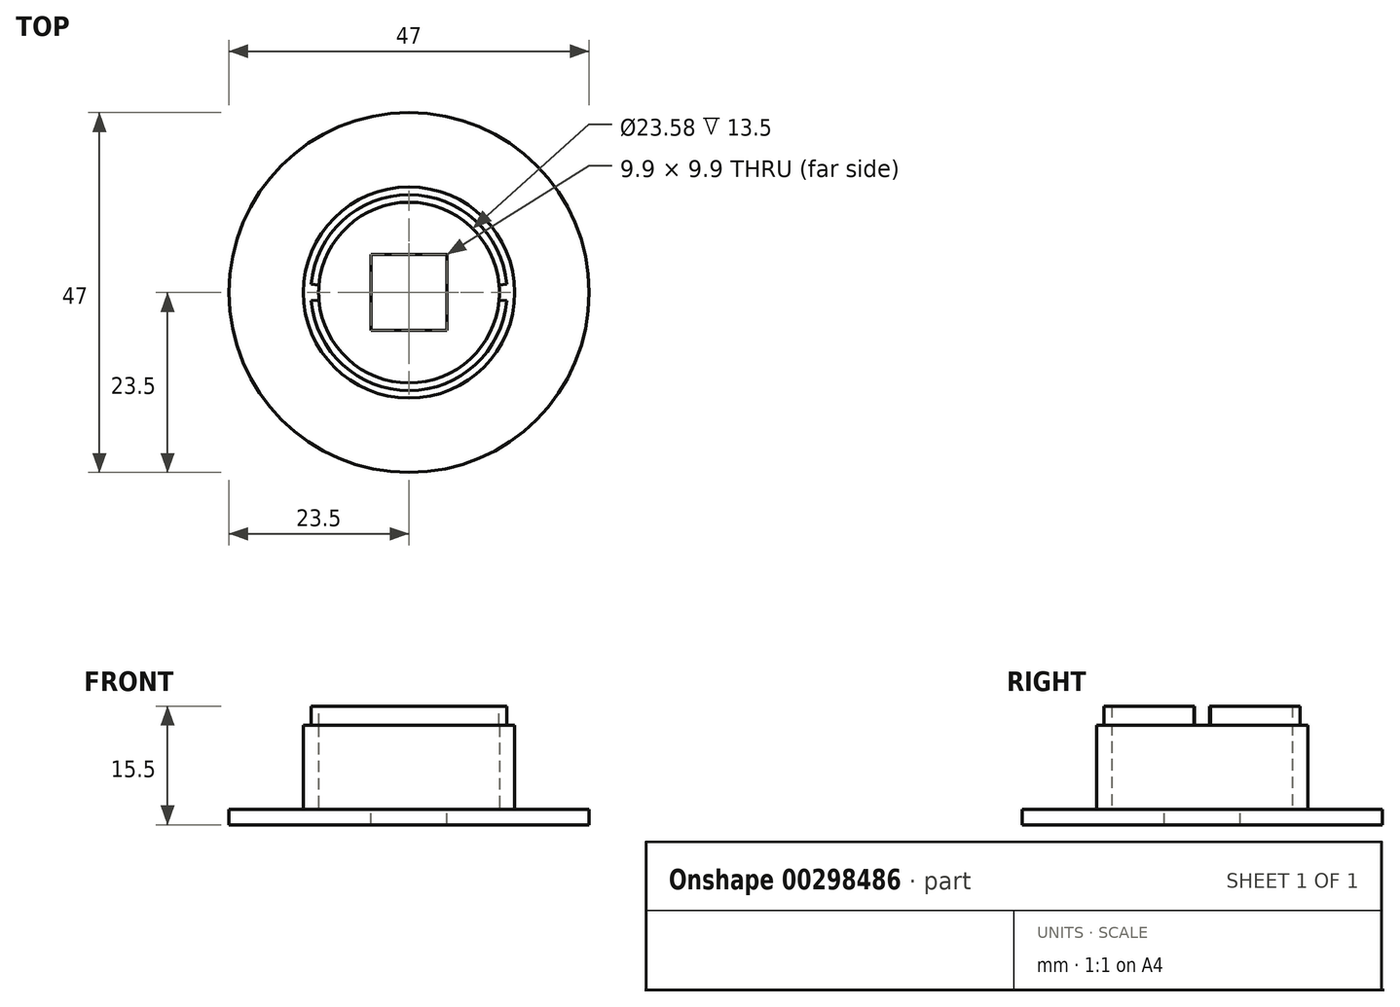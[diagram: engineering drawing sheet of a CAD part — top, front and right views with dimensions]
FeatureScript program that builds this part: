
annotation { "Feature Type Name" : "Feature", "Feature Type Description" : "" }
export const myFeature = defineFeature(function(context is Context, id is Id, definition is map)
    precondition{}
    {
        {
            var Q0;
            Q0=qCreatedBy(makeId("Front.planeOp"),FACE);
            var sketch = newSketch(context, id + "F0", { "sketchPlane" : qUnion([Q0])});
            skLineSegment(sketch, "E0", {"start": v(0, 0) * mm, "end": v(-23.5, 0) * mm});
            skLineSegment(sketch, "E1", {"start": v(-23.5, 0) * mm, "end": v(-23.5, 2) * mm});
            skLineSegment(sketch, "E2", {"start": v(-23.5, 2) * mm, "end": v(-13.8, 2) * mm});
            skLineSegment(sketch, "E3", {"start": v(-13.8, 2) * mm, "end": v(-13.8, 13) * mm});
            skLineSegment(sketch, "E4.top", {"start": v(-13.8, 13) * mm, "end": v(-12.8, 13) * mm});
            skLineSegment(sketch, "E4.right", {"start": v(-12.8, 15.5) * mm, "end": v(-12.8, 13) * mm});
            skLineSegment(sketch, "E5.0", {"start": v(-11.8, 15.5) * mm, "end": v(-11.8, 13) * mm});
            skLineSegment(sketch, "E6", {"start": v(-11.8, 13) * mm, "end": v(-11.8, 2) * mm});
            skLineSegment(sketch, "E7", {"start": v(-11.8, 2) * mm, "end": v(0, 2) * mm});
            skLineSegment(sketch, "E8", {"start": v(0, 0) * mm, "end": v(0, 2) * mm});
            skLineSegment(sketch, "E9", {"start": v(-12.8, 15.5) * mm, "end": v(-11.8, 15.5) * mm});
            skSolve(sketch);
        }
        {
            var Q0;
            Q0=makeQuery(id+"F0.imprint","IMPRINT",FACE,{"disambiguationData":[TD([[makeQuery(id+"F0.imprint","IMPRINT",EDGE,{"derivedFrom":sQuery(id+"F0.wireOp",EDGE,"E0")}),-1.0]])]});
            var Q1;
            Q1=sQuery(id+"F0.wireOp",EDGE,"E8");
            revolve(context, id + "F1", {"entities" : qUnion([Q0]), "axis" : qUnion([Q1]), "revolveType" : RevolveType.FULL});
        }
        {
            var Q0;
            Q0=makeQuery(id+"F1.opRevolve","SWEPT_FACE",FACE,{"disambiguationData":[OSD([sQuery(id+"F0.wireOp",EDGE,"E9")])]});
            var sketch = newSketch(context, id + "F2", { "sketchPlane" : qUnion([Q0])});
            skCircle(sketch, "E10.0.0", {"center": v(0, 0) * mm, "radius": 12.8 * mm});
            skArc(sketch, "E11.0.0", {"start": v(12.74, -1.08) * mm, "mid": v(12.8, 0) * mm, "end": v(12.74, 1.08) * mm});
            skArc(sketch, "E12", {"start": v(-11.75, -1) * mm, "mid": v(-11.8, 0) * mm, "end": v(-11.75, 1) * mm});
            skLineSegment(sketch, "E13", {"start": v(-11.75, 1) * mm, "end": v(-12.74, 1.08) * mm});
            skLineSegment(sketch, "E14.MirrorCS", {"start": v(-11.75, -1) * mm, "end": v(-12.74, -1.08) * mm});
            skLineSegment(sketch, "E15.MirrorCS", {"start": v(11.75, 1) * mm, "end": v(12.74, 1.08) * mm});
            skLineSegment(sketch, "E16.MirrorCS", {"start": v(11.75, -1) * mm, "end": v(12.74, -1.08) * mm});
            skArc(sketch, "E17.trimOffspring", {"start": v(-12.74, 1.08) * mm, "mid": v(-12.8, 0) * mm, "end": v(-12.74, -1.08) * mm});
            skArc(sketch, "E18.trimOffspring", {"start": v(11.75, 1) * mm, "mid": v(11.8, 0) * mm, "end": v(11.75, -1) * mm});
            skSolve(sketch);
        }
        {
            var Q0;
            Q0=makeQuery(id+"F2.imprint","IMPRINT",FACE,{"disambiguationData":[TD([[makeQuery(id+"F2.imprint","IMPRINT",EDGE,{"derivedFrom":sQuery(id+"F2.wireOp",EDGE,"E12")}),1.0]])]});
            var Q1;
            {var subQ0=sQuery(id+"F2.wireOp",EDGE,"E15.MirrorCS");Q1=makeQuery(id+"F2.imprint","IMPRINT",FACE,{"disambiguationData":[TD([[makeQuery(id+"F2.imprint","IMPRINT",EDGE,{"derivedFrom":subQ0}),-1.0]])]});}
            var Q2;
            Q2=makeQuery(id+"F1.opRevolve","SWEPT_FACE",FACE,{"disambiguationData":[OSD([sQuery(id+"F0.wireOp",EDGE,"E4.top")])]});
            extrude(context, id + "F3", {"entities" : qUnion([Q0, Q1]), "operationType" : NewBodyOperationType.REMOVE, "endBound" : BoundingType.UP_TO_SURFACE, "oppositeDirection" : true, "endBoundEntityFace" : qUnion([Q2]), "depth" : 2.5 * mm});
        }
        {
            var Q0;
            Q0=makeQuery(id+"F1.opRevolve","SWEPT_FACE",FACE,{"disambiguationData":[OSD([sQuery(id+"F0.wireOp",EDGE,"E7")])]});
            var sketch = newSketch(context, id + "F4", { "sketchPlane" : qUnion([Q0])});
            skLineSegment(sketch, "E19.bottom", {"start": v(-4.95, 4.95) * mm, "end": v(4.95, 4.95) * mm});
            skLineSegment(sketch, "E19.top", {"start": v(-4.95, -4.95) * mm, "end": v(4.95, -4.95) * mm});
            skLineSegment(sketch, "E19.left", {"start": v(-4.95, 4.95) * mm, "end": v(-4.95, -4.95) * mm});
            skLineSegment(sketch, "E19.right", {"start": v(4.95, 4.95) * mm, "end": v(4.95, -4.95) * mm});
            skPoint(sketch, "E19.middle", {"position": v(0, 0) * mm});
            skSolve(sketch);
        }
        {
            var Q0;
            Q0 = qSketchRegion(id + "F4", true);
            extrude(context, id + "F5", {"entities" : qUnion([Q0]), "operationType" : NewBodyOperationType.REMOVE, "endBound" : BoundingType.THROUGH_ALL, "oppositeDirection" : true, "depth" : 25 * mm});
        }
    });
